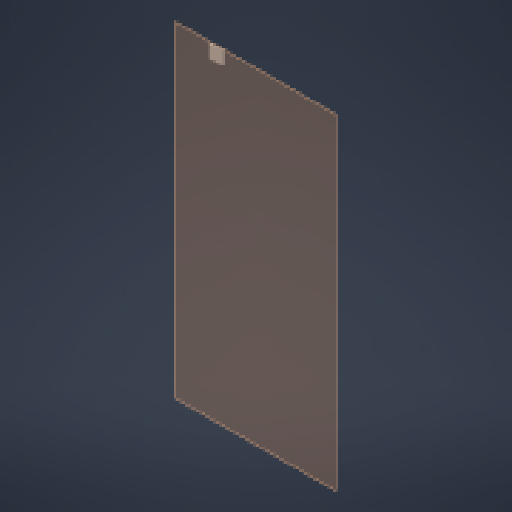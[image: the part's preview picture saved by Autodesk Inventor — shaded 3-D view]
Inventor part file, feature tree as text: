
AUTODESK INVENTOR PART (.ipt)
format: ipt  version: 2024 (Build 280153000, 153)  size: 125,440 bytes
history: native  units: mm
features: other x5, plane x1, extrude x1, sketch x1
ambient origin geometry x8: Origin, YZ Plane, XZ Plane, XY Plane, X Axis, Y Axis, Z Axis, Center Point
bodies: Body1 (feature_tree)
feature tree (8):
  other  "Sólido1"
  plane  "Plano de trabajo1"
  extrude  "Extrusión1"  Depth=30.0mm
  sketch  "Boceto1"  dims[d0=120.0mm d1=30.0mm d2=30.0mm d3=30.0mm d4=2.0mm d5=0.0mm]
  other  "<userpath>\Downloads\Piezas CMR\Marco_APM_001\Marco_apm_001-3.iam"
  other  "Marco_apm_001-3.iam"
  other  "Marco_Conveyor_Aereo:1"
  other  "Marco:1"
